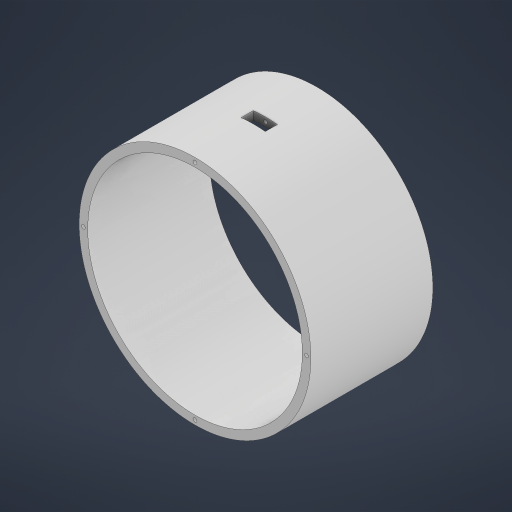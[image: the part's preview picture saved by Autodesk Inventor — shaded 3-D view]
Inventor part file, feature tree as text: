
AUTODESK INVENTOR PART (.ipt)
format: ipt  version: 2023 (Build 270158000, 158)  size: 442,368 bytes
history: native  units: mm
features: extrude x3, sketch x3, plane x2
ambient origin geometry x8: Origin, YZ Plane, XZ Plane, XY Plane, X Axis, Y Axis, Z Axis, Center Point
bodies: Solid1 (feature_tree)
feature tree (8):
  extrude  "Extrusion1"  Depth=7.0mm
  plane  "Work Plane2"
  extrude  "Extrusion3"  Depth=3.0mm
  plane  "Work Plane1"
  extrude  "Extrusion7"  Depth=10.0mm
  sketch  "Sketch1"  dims[d0=190.0mm d3=7.0mm]
  sketch  "Sketch3"  dims[d5=3.0mm d6=3.0mm]
  sketch  "Sketch7"  dims[d7=3.0mm d8=3.0mm d9=100.0mm d10=0.0mm d14=8.0mm d15=135.0deg d16=4.0mm d17=0.0mm d35=3.0mm d37=3.0mm d39=10.0mm d40=150.0mm d41=0.0mm d42=4.982mm d43=90.0deg]
